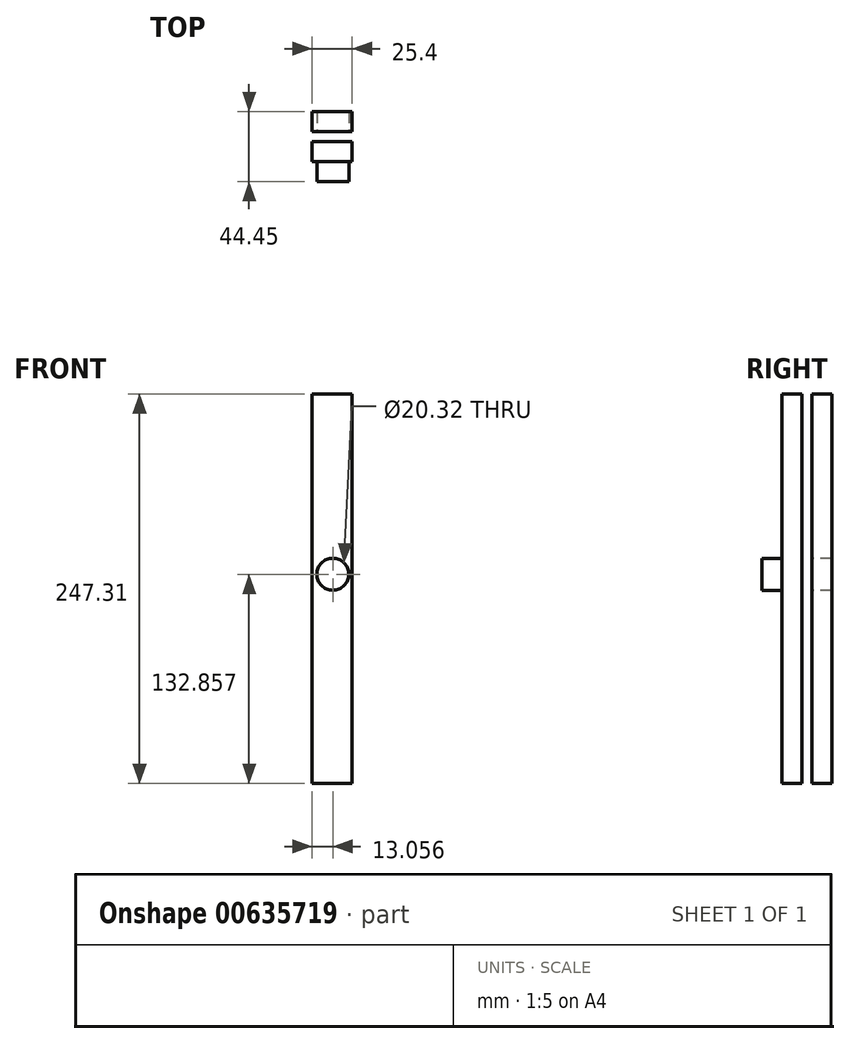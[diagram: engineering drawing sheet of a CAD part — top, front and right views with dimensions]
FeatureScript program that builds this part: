
annotation { "Feature Type Name" : "Feature", "Feature Type Description" : "" }
export const myFeature = defineFeature(function(context is Context, id is Id, definition is map)
    precondition{}
    {
        {
            var Q0;
            Q0=qCreatedBy(makeId("Front.planeOp"),FACE);
            var sketch = newSketch(context, id + "F0", { "sketchPlane" : qUnion([Q0])});
            skCircle(sketch, "E0", {"center": v(13.06, -14.34) * mm, "radius": 10.16 * mm});
            skLineSegment(sketch, "E1", {"start": v(25.4, 100.1) * mm, "end": v(25.4, -147.2) * mm});
            skLineSegment(sketch, "E2", {"start": v(0, 100.1) * mm, "end": v(0, -147.2) * mm});
            skLineSegment(sketch, "E3", {"start": v(0, -147.2) * mm, "end": v(0, 100.1) * mm});
            skLineSegment(sketch, "E4", {"start": v(25.4, 100.1) * mm, "end": v(0, 100.1) * mm});
            skLineSegment(sketch, "E5", {"start": v(25.4, -147.2) * mm, "end": v(0, -147.2) * mm});
            skSolve(sketch);
        }
        {
            var Q0;
            Q0=makeQuery(id+"F0.imprint","IMPRINT",FACE,{"disambiguationData":[TD([[makeQuery(id+"F0.imprint","IMPRINT",EDGE,{"derivedFrom":sQuery(id+"F0.wireOp",EDGE,"E0")}),-1.0]])]});
            extrude(context, id + "F1", {"entities" : qUnion([Q0]), "depth" : 12.7 * mm, "offsetDistance" : 25.4 * mm});
        }
        {
            var Q0;
            Q0=makeQuery(id+"F0.imprint","IMPRINT",FACE,{"disambiguationData":[TD([[makeQuery(id+"F0.imprint","IMPRINT",EDGE,{"derivedFrom":sQuery(id+"F0.wireOp",EDGE,"E0")}),1.0]])]});
            extrude(context, id + "F2", {"entities" : qUnion([Q0]), "operationType" : NewBodyOperationType.ADD, "depth" : 25.4 * mm, "offsetDistance" : 25.4 * mm});
        }
        {
            var Q0;
            Q0=makeQuery(id+"F0.imprint","IMPRINT",FACE,{"disambiguationData":[TD([[makeQuery(id+"F0.imprint","IMPRINT",EDGE,{"derivedFrom":sQuery(id+"F0.wireOp",EDGE,"E0")}),-1.0]])]});
            extrude(context, id + "F3", {"entities" : qUnion([Q0]), "oppositeDirection" : true, "depth" : 19.05 * mm, "offsetDistance" : 25.4 * mm});
        }
        {
            var Q0;
            Q0=makeQuery(id+"F0.imprint","IMPRINT",FACE,{"disambiguationData":[TD([[makeQuery(id+"F0.imprint","IMPRINT",EDGE,{"derivedFrom":sQuery(id+"F0.wireOp",EDGE,"E0")}),-1.0]])]});
            extrude(context, id + "F4", {"entities" : qUnion([Q0]), "operationType" : NewBodyOperationType.REMOVE, "oppositeDirection" : true, "depth" : 6.35 * mm, "offsetDistance" : 25.4 * mm});
        }
    });
